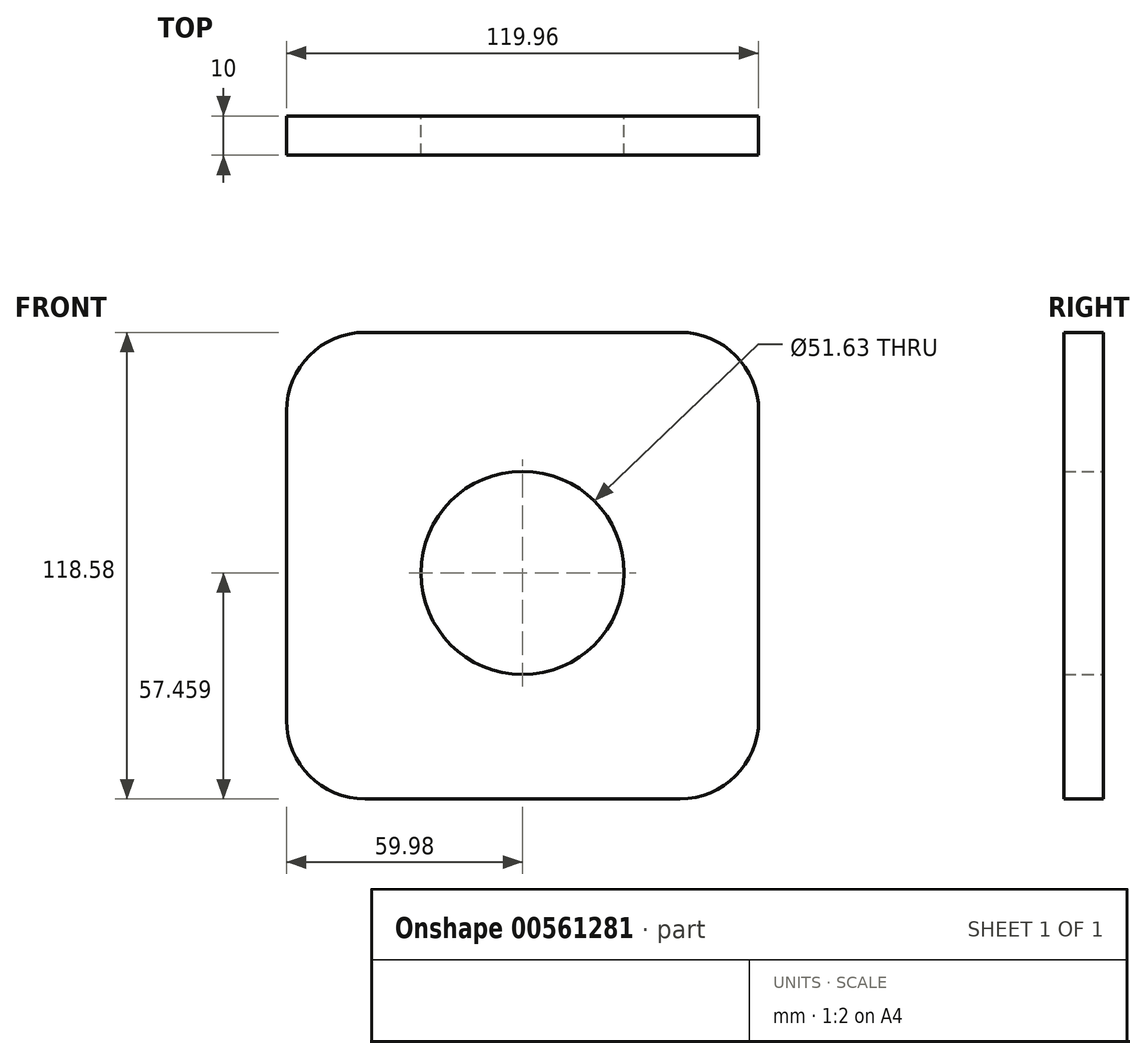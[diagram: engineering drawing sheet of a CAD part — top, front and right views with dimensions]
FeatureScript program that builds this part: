
annotation { "Feature Type Name" : "Feature", "Feature Type Description" : "" }
export const myFeature = defineFeature(function(context is Context, id is Id, definition is map)
    precondition{}
    {
        {
            var Q0;
            Q0=qCreatedBy(makeId("Front.planeOp"),FACE);
            var sketch = newSketch(context, id + "F0", { "sketchPlane" : qUnion([Q0])});
            skLineSegment(sketch, "E0.bottom", {"start": v(-59.98, 59.3) * mm, "end": v(59.98, 59.3) * mm});
            skLineSegment(sketch, "E0.top", {"start": v(-59.98, -59.3) * mm, "end": v(59.98, -59.3) * mm});
            skLineSegment(sketch, "E0.left", {"start": v(-59.98, 59.3) * mm, "end": v(-59.98, -59.3) * mm});
            skLineSegment(sketch, "E0.right", {"start": v(59.98, 59.3) * mm, "end": v(59.98, -59.3) * mm});
            skPoint(sketch, "E0.middle", {"position": v(0, 0) * mm});
            skCircle(sketch, "E1", {"center": v(0, -1.83) * mm, "radius": 25.82 * mm});
            skSolve(sketch);
        }
        {
            var Q0;
            Q0=makeQuery(id+"F0.imprint","IMPRINT",FACE,{"disambiguationData":[TD([[makeQuery(id+"F0.imprint","IMPRINT",EDGE,{"derivedFrom":sQuery(id+"F0.wireOp",EDGE,"E0.bottom")}),-1.0]])]});
            extrude(context, id + "F1", {"entities" : qUnion([Q0]), "depth" : 10 * mm, "offsetDistance" : 25 * mm});
        }
        {
            var Q0;
            Q0=makeQuery(id+"F1.opExtrude","SWEPT_EDGE",EDGE,{"disambiguationData":[OSD([sQuery(id+"F0.wireOp",EDGE,"E0.bottom"),sQuery(id+"F0.wireOp",EDGE,"E0.left")])]});
            var Q1;
            Q1=makeQuery(id+"F1.opExtrude","SWEPT_EDGE",EDGE,{"disambiguationData":[OSD([sQuery(id+"F0.wireOp",EDGE,"E0.bottom"),sQuery(id+"F0.wireOp",EDGE,"E0.right")])]});
            var Q2;
            Q2=makeQuery(id+"F1.opExtrude","SWEPT_EDGE",EDGE,{"disambiguationData":[OSD([sQuery(id+"F0.wireOp",EDGE,"E0.top"),sQuery(id+"F0.wireOp",EDGE,"E0.left")])]});
            var Q3;
            Q3=makeQuery(id+"F1.opExtrude","SWEPT_EDGE",EDGE,{"disambiguationData":[OSD([sQuery(id+"F0.wireOp",EDGE,"E0.top"),sQuery(id+"F0.wireOp",EDGE,"E0.right")])]});
            fillet(context, id + "F2", {"entities" : qUnion([Q0, Q1, Q2, Q3]), "radius" : 20 * mm, "tangentPropagation" : true, "allowEdgeOverflow" : false});
        }
    });
